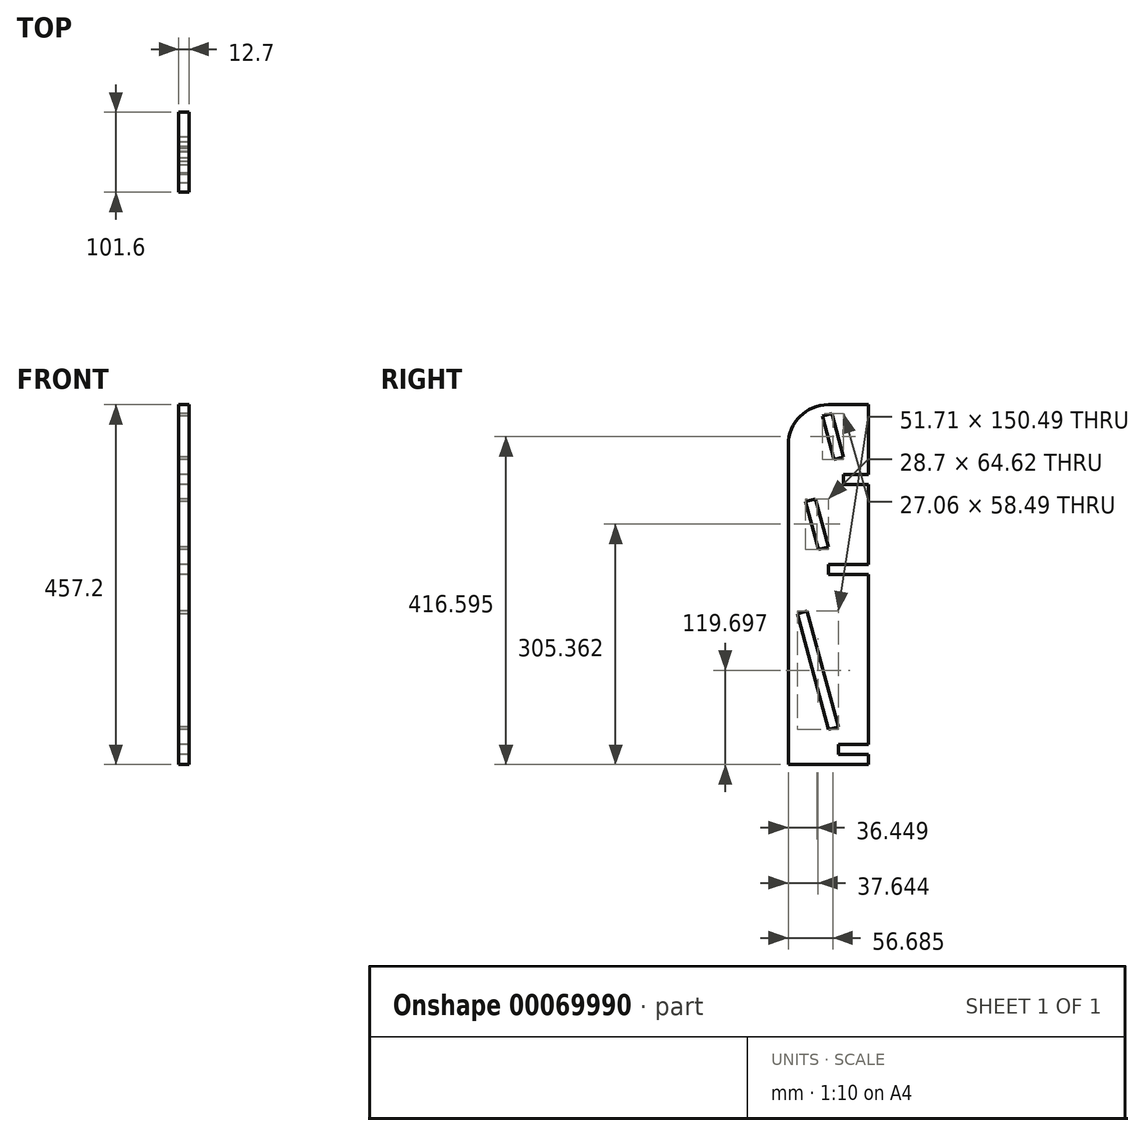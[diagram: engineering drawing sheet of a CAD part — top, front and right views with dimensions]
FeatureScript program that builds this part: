
annotation { "Feature Type Name" : "Feature", "Feature Type Description" : "" }
export const myFeature = defineFeature(function(context is Context, id is Id, definition is map)
    precondition{}
    {
        {
            var Q0;
            Q0=qCreatedBy(makeId("Right.planeOp"),FACE);
            var sketch = newSketch(context, id + "F0", { "sketchPlane" : qUnion([Q0])});
            skLineSegment(sketch, "E0", {"start": v(0, 0) * mm, "end": v(-101.6, 0) * mm});
            skLineSegment(sketch, "E1", {"start": v(-101.6, 0) * mm, "end": v(-101.6, 406.4) * mm});
            skLineSegment(sketch, "E2", {"start": v(-50.8, 457.2) * mm, "end": v(0, 457.2) * mm});
            skLineSegment(sketch, "E3", {"start": v(0, 457.2) * mm, "end": v(0, 0) * mm});
            skPoint(sketch, "E4.visualSharp", {"position": v(-101.6, 457.2) * mm});
            skArc(sketch, "E4.filletArc", {"start": v(-50.8, 457.2) * mm, "mid": v(-86.72, 442.32) * mm, "end": v(-101.6, 406.4) * mm});
            skLineSegment(sketch, "E5", {"start": v(-38.1, 12.7) * mm, "end": v(-38.1, 25.4) * mm});
            skLineSegment(sketch, "E6.MirrorCS", {"start": v(0, 12.7) * mm, "end": v(-38.1, 12.7) * mm});
            skLineSegment(sketch, "E7.MirrorCS", {"start": v(-38.1, 25.4) * mm, "end": v(0, 25.4) * mm});
            skLineSegment(sketch, "E8", {"start": v(-38.1, 25.4) * mm, "end": v(-38.1, 25.4) * mm});
            skLineSegment(sketch, "E9", {"start": v(-12.7, 0) * mm, "end": v(-12.7, 457.2) * mm, "construction": true});
            skLineSegment(sketch, "E10", {"start": v(-38.1, 47.74) * mm, "end": v(-77.54, 194.94) * mm});
            skLineSegment(sketch, "E11", {"start": v(-77.54, 194.94) * mm, "end": v(-89.81, 191.66) * mm});
            skLineSegment(sketch, "E12", {"start": v(-89.81, 191.66) * mm, "end": v(-50.37, 44.45) * mm});
            skLineSegment(sketch, "E13", {"start": v(-50.37, 44.45) * mm, "end": v(-38.1, 47.74) * mm});
            skLineSegment(sketch, "E14", {"start": v(-38.1, 47.74) * mm, "end": v(-32.11, 25.4) * mm, "construction": true});
            skLineSegment(sketch, "E15", {"start": v(-79.5, 334.39) * mm, "end": v(-63.07, 273.05) * mm});
            skLineSegment(sketch, "E16", {"start": v(-50.8, 276.34) * mm, "end": v(-67.24, 337.67) * mm});
            skLineSegment(sketch, "E17.MirrorCS", {"start": v(0, 241.3) * mm, "end": v(-50.8, 241.3) * mm});
            skLineSegment(sketch, "E18.MirrorCS", {"start": v(-50.8, 254) * mm, "end": v(0, 254) * mm});
            skLineSegment(sketch, "E19", {"start": v(-50.8, 254) * mm, "end": v(-50.8, 254) * mm});
            skLineSegment(sketch, "E20", {"start": v(-50.8, 276.34) * mm, "end": v(-44.81, 254) * mm, "construction": true});
            skLineSegment(sketch, "E21", {"start": v(-50.8, 241.3) * mm, "end": v(-50.8, 254) * mm});
            skLineSegment(sketch, "E22", {"start": v(-67.24, 337.67) * mm, "end": v(-79.5, 334.39) * mm});
            skLineSegment(sketch, "E23", {"start": v(-63.07, 273.05) * mm, "end": v(-50.8, 276.34) * mm});
            skLineSegment(sketch, "E24", {"start": v(-50.8, 254) * mm, "end": v(-50.8, 241.3) * mm, "construction": true});
            skLineSegment(sketch, "E25", {"start": v(-50.8, 241.3) * mm, "end": v(-50.8, 241.3) * mm});
            skLineSegment(sketch, "E26", {"start": v(-38.1, 25.4) * mm, "end": v(-38.1, 12.7) * mm, "construction": true});
            skLineSegment(sketch, "E27", {"start": v(-38.1, 12.7) * mm, "end": v(-38.1, 12.7) * mm});
            skLineSegment(sketch, "E28.MirrorCS", {"start": v(0, 355.6) * mm, "end": v(-31.75, 355.6) * mm});
            skLineSegment(sketch, "E29", {"start": v(-31.39, 390.64) * mm, "end": v(-25.4, 368.3) * mm, "construction": true});
            skLineSegment(sketch, "E30", {"start": v(-31.75, 368.3) * mm, "end": v(-31.75, 368.3) * mm});
            skLineSegment(sketch, "E31", {"start": v(-31.75, 355.6) * mm, "end": v(-31.75, 355.6) * mm});
            skLineSegment(sketch, "E32", {"start": v(-58.44, 442.55) * mm, "end": v(-43.65, 387.35) * mm});
            skLineSegment(sketch, "E33.MirrorCS", {"start": v(-31.75, 368.3) * mm, "end": v(0, 368.3) * mm});
            skLineSegment(sketch, "E34", {"start": v(-31.39, 390.64) * mm, "end": v(-46.18, 445.84) * mm});
            skLineSegment(sketch, "E35", {"start": v(-43.65, 387.35) * mm, "end": v(-31.39, 390.64) * mm});
            skLineSegment(sketch, "E36", {"start": v(-46.18, 445.84) * mm, "end": v(-58.44, 442.55) * mm});
            skLineSegment(sketch, "E37", {"start": v(-31.75, 368.3) * mm, "end": v(-31.75, 355.6) * mm, "construction": true});
            skLineSegment(sketch, "E38", {"start": v(-31.75, 355.6) * mm, "end": v(-31.75, 368.3) * mm});
            skSolve(sketch);
        }
        {
            var Q0;
            {var subQ5=sQuery(id+"F0.wireOp",EDGE,"E0");Q0=makeQuery(id+"F0.imprint","IMPRINT",FACE,{"disambiguationData":[TD([[makeQuery(id+"F0.imprint","IMPRINT",EDGE,{"derivedFrom":subQ5}),-1.0]])]});}
            extrude(context, id + "F1", {"entities" : qUnion([Q0]), "depth" : 12.7 * mm});
        }
    });
